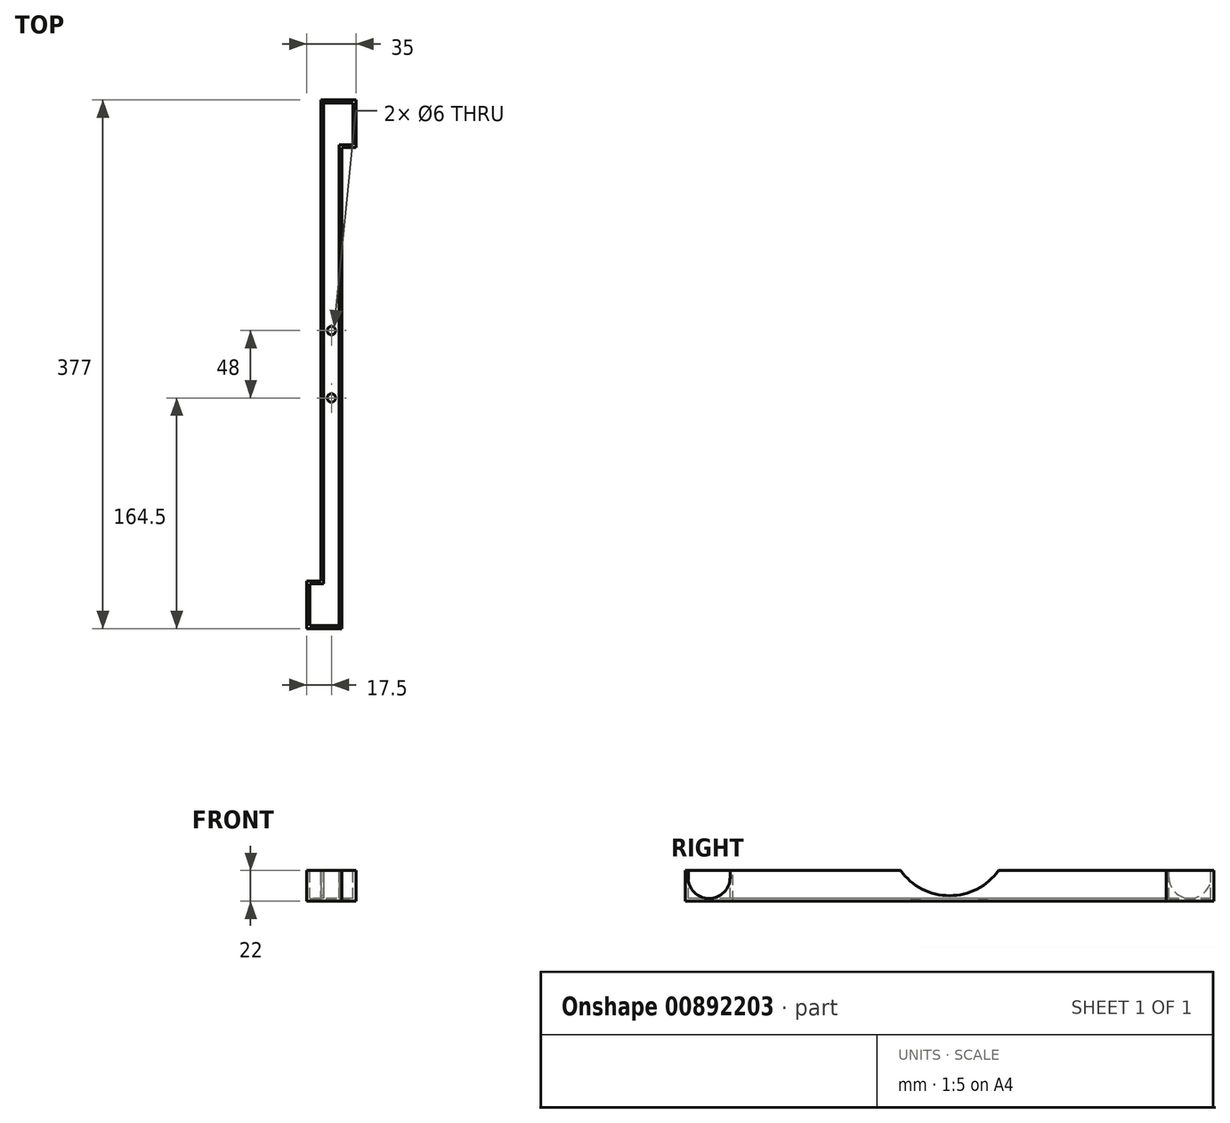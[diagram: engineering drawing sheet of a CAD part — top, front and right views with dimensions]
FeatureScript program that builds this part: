
annotation { "Feature Type Name" : "Feature", "Feature Type Description" : "" }
export const myFeature = defineFeature(function(context is Context, id is Id, definition is map)
    precondition{}
    {
        {
            var Q0;
            Q0=qCreatedBy(makeId("Top.planeOp"),FACE);
            var sketch = newSketch(context, id + "F0", { "sketchPlane" : qUnion([Q0])});
            skLineSegment(sketch, "E0", {"start": v(0, 313) * mm, "end": v(10, 313) * mm});
            skLineSegment(sketch, "E1", {"start": v(10, 313) * mm, "end": v(10, 343) * mm});
            skLineSegment(sketch, "E2", {"start": v(10, 343) * mm, "end": v(-11, 343) * mm});
            skLineSegment(sketch, "E3", {"start": v(-11, 0) * mm, "end": v(-21, 0) * mm});
            skLineSegment(sketch, "E4", {"start": v(-21, 0) * mm, "end": v(-21, -30) * mm});
            skLineSegment(sketch, "E5", {"start": v(-21, -30) * mm, "end": v(0, -30) * mm});
            skLineSegment(sketch, "E6", {"start": v(0, 313) * mm, "end": v(0, -30) * mm});
            skLineSegment(sketch, "E7", {"start": v(-11, 343) * mm, "end": v(-11, 0) * mm});
            skLineSegment(sketch, "E8.0", {"start": v(12, 311) * mm, "end": v(12, 345) * mm});
            skLineSegment(sketch, "E8.1", {"start": v(2, 311) * mm, "end": v(12, 311) * mm});
            skLineSegment(sketch, "E8.2", {"start": v(12, 345) * mm, "end": v(-13, 345) * mm});
            skLineSegment(sketch, "E8.3", {"start": v(2, 311) * mm, "end": v(2, -32) * mm});
            skLineSegment(sketch, "E8.4", {"start": v(-13, 345) * mm, "end": v(-13, 2) * mm});
            skLineSegment(sketch, "E8.5", {"start": v(-13, 2) * mm, "end": v(-23, 2) * mm});
            skLineSegment(sketch, "E8.6", {"start": v(-23, 2) * mm, "end": v(-23, -32) * mm});
            skLineSegment(sketch, "E8.7", {"start": v(-23, -32) * mm, "end": v(2, -32) * mm});
            skCircle(sketch, "E9", {"center": v(-5.5, 180.5) * mm, "radius": 3 * mm});
            skCircle(sketch, "E10", {"center": v(-5.5, 132.5) * mm, "radius": 3 * mm});
            skLineSegment(sketch, "E11", {"start": v(-5.5, 132.5) * mm, "end": v(-5.5, 180.5) * mm});
            skLineSegment(sketch, "E12", {"start": v(-5.5, 156.5) * mm, "end": v(-23.68, 156.5) * mm});
            skSolve(sketch);
        }
        {
            var Q0;
            Q0=makeQuery(id+"F0.imprint","IMPRINT",FACE,{"disambiguationData":[TD([[makeQuery(id+"F0.imprint","IMPRINT",EDGE,{"derivedFrom":sQuery(id+"F0.wireOp",EDGE,"E0")}),-1.0]])]});
            var Q1;
            Q1=makeQuery(id+"F0.imprint","IMPRINT",FACE,{"disambiguationData":[TD([[makeQuery(id+"F0.imprint","IMPRINT",EDGE,{"derivedFrom":sQuery(id+"F0.wireOp",EDGE,"E0")}),1.0]])]});
            extrude(context, id + "F1", {"entities" : qUnion([Q0, Q1]), "oppositeDirection" : true, "depth" : 22 * mm, "offsetDistance" : 25 * mm});
        }
        {
            var Q0;
            Q0=makeQuery(id+"F1.opExtrude","SWEPT_FACE",FACE,{"disambiguationData":[OSD([sQuery(id+"F0.wireOp",EDGE,"E8.4")])]});
            var sketch = newSketch(context, id + "F2", { "sketchPlane" : qUnion([Q0])});
            skArc(sketch, "E13", {"start": v(-343, -5) * mm, "mid": v(-328, -19.95) * mm, "end": v(-313, -5) * mm});
            skLineSegment(sketch, "E14", {"start": v(-343, -5) * mm, "end": v(-343.02, 0) * mm});
            skLineSegment(sketch, "E15", {"start": v(-313, -5) * mm, "end": v(-313, 0) * mm});
            skLineSegment(sketch, "E16", {"start": v(-343.02, 0) * mm, "end": v(-313, 0) * mm});
            skSolve(sketch);
        }
        {
            var Q0;
            Q0=makeQuery(id+"F0.imprint","IMPRINT",FACE,{"disambiguationData":[TD([[makeQuery(id+"F0.imprint","IMPRINT",EDGE,{"derivedFrom":sQuery(id+"F0.wireOp",EDGE,"E0")}),1.0]])]});
            extrude(context, id + "F3", {"entities" : qUnion([Q0]), "operationType" : NewBodyOperationType.REMOVE, "oppositeDirection" : true, "depth" : 20 * mm, "offsetDistance" : 25 * mm});
        }
        {
            var Q0;
            Q0=makeQuery(id+"F1.opExtrude","SWEPT_FACE",FACE,{"disambiguationData":[OSD([sQuery(id+"F0.wireOp",EDGE,"E8.3")])]});
            var sketch = newSketch(context, id + "F4", { "sketchPlane" : qUnion([Q0])});
            skLineSegment(sketch, "E17", {"start": v(-32, 0) * mm, "end": v(-30.1, 0) * mm});
            skLineSegment(sketch, "E18", {"start": v(-30.1, 0) * mm, "end": v(-30.1, -5) * mm});
            skLineSegment(sketch, "E19", {"start": v(-30.1, 0) * mm, "end": v(-0.1, 0) * mm});
            skLineSegment(sketch, "E20", {"start": v(-0.1, 0) * mm, "end": v(-0.1, -5) * mm});
            skArc(sketch, "E21", {"start": v(-30.1, -5) * mm, "mid": v(-15.1, -20) * mm, "end": v(-0.1, -5) * mm});
            skSolve(sketch);
        }
        {
            var Q0;
            Q0=makeQuery(id+"F4.imprint","IMPRINT",FACE,{"disambiguationData":[TD([[makeQuery(id+"F4.imprint","IMPRINT",EDGE,{"derivedFrom":sQuery(id+"F4.wireOp",EDGE,"E18")}),1.0]])]});
            extrude(context, id + "F5", {"entities" : qUnion([Q0]), "operationType" : NewBodyOperationType.REMOVE, "oppositeDirection" : true, "depth" : 2 * mm, "offsetDistance" : 25 * mm});
        }
        {
            var Q0;
            Q0=makeQuery(id+"F2.imprint","IMPRINT",FACE,{"disambiguationData":[TD([[makeQuery(id+"F2.imprint","IMPRINT",EDGE,{"derivedFrom":sQuery(id+"F2.wireOp",EDGE,"E13")}),1.0]])]});
            extrude(context, id + "F6", {"entities" : qUnion([Q0]), "operationType" : NewBodyOperationType.REMOVE, "oppositeDirection" : true, "depth" : 2 * mm, "offsetDistance" : 25 * mm});
        }
        {
            var Q0;
            Q0=makeQuery(id+"F0.imprint","IMPRINT",FACE,{"disambiguationData":[TD([[makeQuery(id+"F0.imprint","IMPRINT",EDGE,{"derivedFrom":sQuery(id+"F0.wireOp",EDGE,"E9")}),1.0]])]});
            var Q1;
            Q1=makeQuery(id+"F0.imprint","IMPRINT",FACE,{"disambiguationData":[TD([[makeQuery(id+"F0.imprint","IMPRINT",EDGE,{"derivedFrom":sQuery(id+"F0.wireOp",EDGE,"b3W9sGt7-y83i-eLEr-evBe-fmybfYgUqKLv")}),1.0]])]});
            extrude(context, id + "F7", {"entities" : qUnion([Q0, Q1]), "operationType" : NewBodyOperationType.REMOVE, "oppositeDirection" : true, "depth" : 22 * mm, "offsetDistance" : 25 * mm});
        }
        {
            var Q0;
            Q0=makeQuery(id+"F1.opExtrude","SWEPT_FACE",FACE,{"disambiguationData":[OSD([sQuery(id+"F0.wireOp",EDGE,"E8.4")])]});
            var sketch = newSketch(context, id + "F8", { "sketchPlane" : qUnion([Q0])});
            skLineSegment(sketch, "E22", {"start": v(-121.5, 0) * mm, "end": v(-156.5, 0) * mm});
            skLineSegment(sketch, "E23.MirrorCS", {"start": v(-191.5, 0) * mm, "end": v(-156.5, 0) * mm});
            skArc(sketch, "E24", {"start": v(-191.5, 0) * mm, "mid": v(-156.5, -18) * mm, "end": v(-121.5, 0) * mm});
            skSolve(sketch);
        }
        {
            var Q0;
            Q0=makeQuery(id+"F8.imprint","IMPRINT",FACE,{"disambiguationData":[TD([[makeQuery(id+"F8.imprint","IMPRINT",EDGE,{"derivedFrom":sQuery(id+"F8.wireOp",EDGE,"E22")}),-1.0]])]});
            extrude(context, id + "F9", {"entities" : qUnion([Q0]), "operationType" : NewBodyOperationType.REMOVE, "oppositeDirection" : true, "depth" : 15 * mm, "offsetDistance" : 25 * mm});
        }
    });
